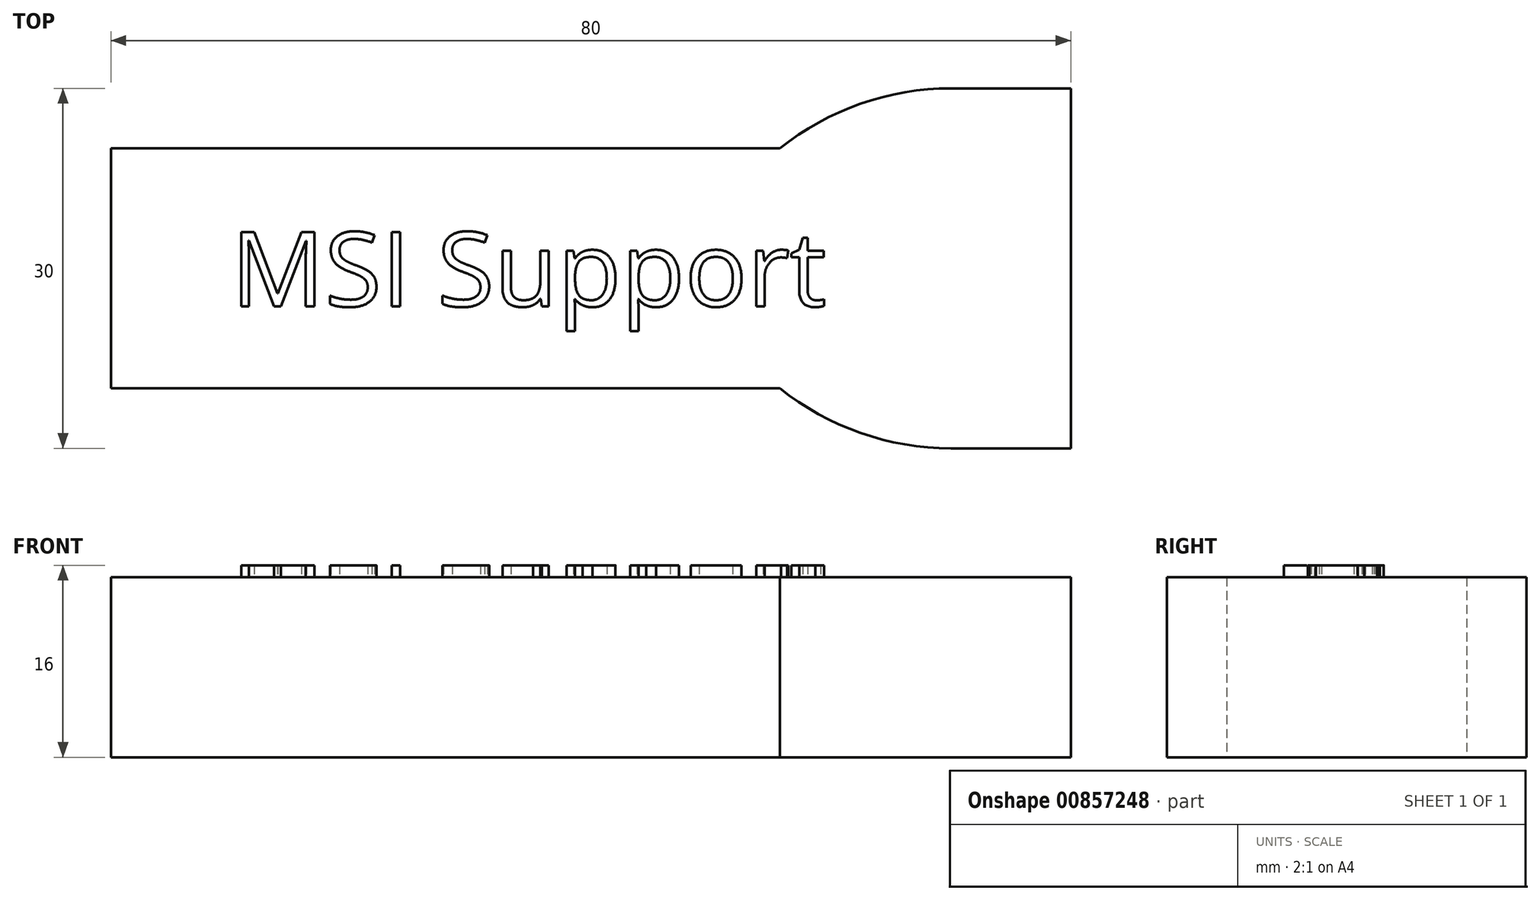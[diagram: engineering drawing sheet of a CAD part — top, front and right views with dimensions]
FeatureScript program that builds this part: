
annotation { "Feature Type Name" : "Feature", "Feature Type Description" : "" }
export const myFeature = defineFeature(function(context is Context, id is Id, definition is map)
    precondition{}
    {
        {
            var Q0;
            Q0=qCreatedBy(makeId("Top.planeOp"),FACE);
            var sketch = newSketch(context, id + "F0", { "sketchPlane" : qUnion([Q0])});
            skLineSegment(sketch, "E0.bottom", {"start": v(-35, 10) * mm, "end": v(35, 10) * mm});
            skLineSegment(sketch, "E0.top", {"start": v(-35, -10) * mm, "end": v(35, -10) * mm});
            skLineSegment(sketch, "E0.left", {"start": v(-35, 10) * mm, "end": v(-35, -10) * mm});
            skLineSegment(sketch, "E0.right", {"start": v(35, 10) * mm, "end": v(35, -10) * mm});
            skPoint(sketch, "E0.middle", {"position": v(0, 0) * mm});
            skLineSegment(sketch, "E1.bottom", {"start": v(35, -15) * mm, "end": v(45, -15) * mm});
            skLineSegment(sketch, "E1.top", {"start": v(35, 15) * mm, "end": v(45, 15) * mm});
            skLineSegment(sketch, "E1.left", {"start": v(35, -15) * mm, "end": v(35, 15) * mm});
            skLineSegment(sketch, "E1.right", {"start": v(45, -15) * mm, "end": v(45, 15) * mm});
            skPoint(sketch, "E1.middle", {"position": v(40, 0) * mm});
            skArc(sketch, "E2", {"start": v(35, 15) * mm, "mid": v(27.46, 13.71) * mm, "end": v(20.77, 10) * mm});
            skArc(sketch, "E3", {"start": v(35, -15) * mm, "mid": v(27.46, -13.71) * mm, "end": v(20.77, -10) * mm});
            skSolve(sketch);
        }
        {
            var Q0;
            Q0 = qSketchRegion(id + "F0", true);
            extrude(context, id + "F1", {"entities" : qUnion([Q0]), "depth" : 15 * mm, "offsetDistance" : 25 * mm});
        }
        {
            var Q0;
            Q0=qCreatedBy(makeId("Top.planeOp"),FACE);
            var sketch = newSketch(context, id + "F2", { "sketchPlane" : qUnion([Q0])});
            skText(sketch, "E4", { "text": "MSI Support", "fontName": "OpenSans-Regular.ttf"});
            const initialGuessF2  = {"E4": [-0.025, -0.00316, 1, 0, 0.00622]};
            skSetInitialGuess(sketch, initialGuessF2);
            skSolve(sketch);
        }
        {
            var Q0;
            Q0 = qSketchRegion(id + "F2", true);
            extrude(context, id + "F3", {"entities" : qUnion([Q0]), "operationType" : NewBodyOperationType.ADD, "depth" : 16 * mm, "offsetDistance" : 25 * mm});
        }
    });
